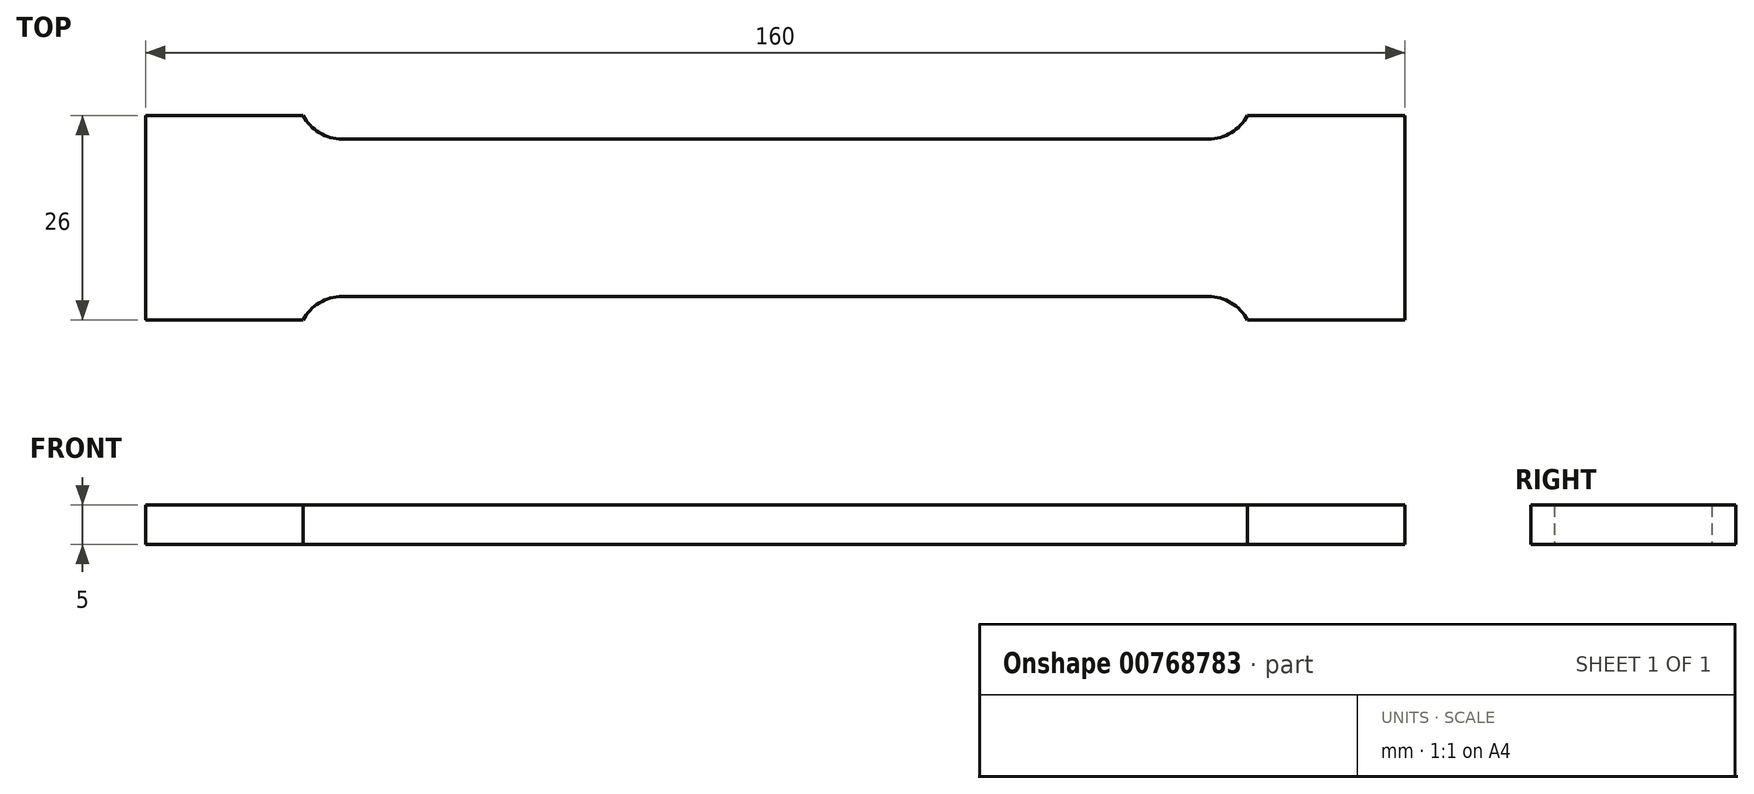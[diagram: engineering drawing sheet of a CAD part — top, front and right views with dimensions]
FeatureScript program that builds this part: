
annotation { "Feature Type Name" : "Feature", "Feature Type Description" : "" }
export const myFeature = defineFeature(function(context is Context, id is Id, definition is map)
    precondition{}
    {
        {
            var Q0;
            Q0=qCreatedBy(makeId("Top.planeOp"),FACE);
            var sketch = newSketch(context, id + "F0", { "sketchPlane" : qUnion([Q0])});
            skLineSegment(sketch, "E0", {"start": v(60, -13) * mm, "end": v(80, -13) * mm});
            skLineSegment(sketch, "E1", {"start": v(80, -13) * mm, "end": v(80, 13) * mm});
            skLineSegment(sketch, "E2", {"start": v(80, 13) * mm, "end": v(60, 13) * mm});
            skLineSegment(sketch, "E3", {"start": v(55, 10) * mm, "end": v(-55, 10) * mm});
            skLineSegment(sketch, "E4", {"start": v(55, -10) * mm, "end": v(-55, -10) * mm});
            skLineSegment(sketch, "E5", {"start": v(-60, 13) * mm, "end": v(-80, 13) * mm});
            skLineSegment(sketch, "E6", {"start": v(-80, 13) * mm, "end": v(-80, -13) * mm});
            skLineSegment(sketch, "E7", {"start": v(-80, -13) * mm, "end": v(-60, -13) * mm});
            skLineSegment(sketch, "E8", {"start": v(84.5, 0) * mm, "end": v(-100.51, 0) * mm});
            skLineSegment(sketch, "E9", {"start": v(0, 16.94) * mm, "end": v(0, -21.9) * mm});
            skArc(sketch, "E10", {"start": v(-55, -10) * mm, "mid": v(-57.91, -10.8) * mm, "end": v(-60, -13) * mm});
            skArc(sketch, "E11", {"start": v(-60, 13) * mm, "mid": v(-57.91, 10.8) * mm, "end": v(-55, 10) * mm});
            skArc(sketch, "E12", {"start": v(55, 10) * mm, "mid": v(57.92, 10.8) * mm, "end": v(60, 13) * mm});
            skArc(sketch, "E13", {"start": v(60, -13) * mm, "mid": v(57.91, -10.8) * mm, "end": v(55, -10) * mm});
            skSolve(sketch);
        }
        {
            var Q0;
            {var subQ5=sQuery(id+"F0.wireOp",EDGE,"E7");Q0=makeQuery(id+"F0.imprint","IMPRINT",FACE,{"disambiguationData":[TD([[makeQuery(id+"F0.imprint","IMPRINT",EDGE,{"derivedFrom":subQ5}),1.0]])]});}
            var Q1;
            {var subQ5=sQuery(id+"F0.wireOp",EDGE,"E0");Q1=makeQuery(id+"F0.imprint","IMPRINT",FACE,{"disambiguationData":[TD([[makeQuery(id+"F0.imprint","IMPRINT",EDGE,{"derivedFrom":subQ5}),1.0]])]});}
            var Q2;
            {var subQ1=sQuery(id+"F0.wireOp",EDGE,"E5");Q2=makeQuery(id+"F0.imprint","IMPRINT",FACE,{"disambiguationData":[TD([[makeQuery(id+"F0.imprint","IMPRINT",EDGE,{"derivedFrom":subQ1}),1.0]])]});}
            var Q3;
            {var subQ4=sQuery(id+"F0.wireOp",EDGE,"E2");Q3=makeQuery(id+"F0.imprint","IMPRINT",FACE,{"disambiguationData":[TD([[makeQuery(id+"F0.imprint","IMPRINT",EDGE,{"derivedFrom":subQ4}),1.0]])]});}
            extrude(context, id + "F1", {"entities" : qUnion([Q0, Q1, Q2, Q3]), "depth" : 5 * mm, "offsetDistance" : 25 * mm});
        }
    });
